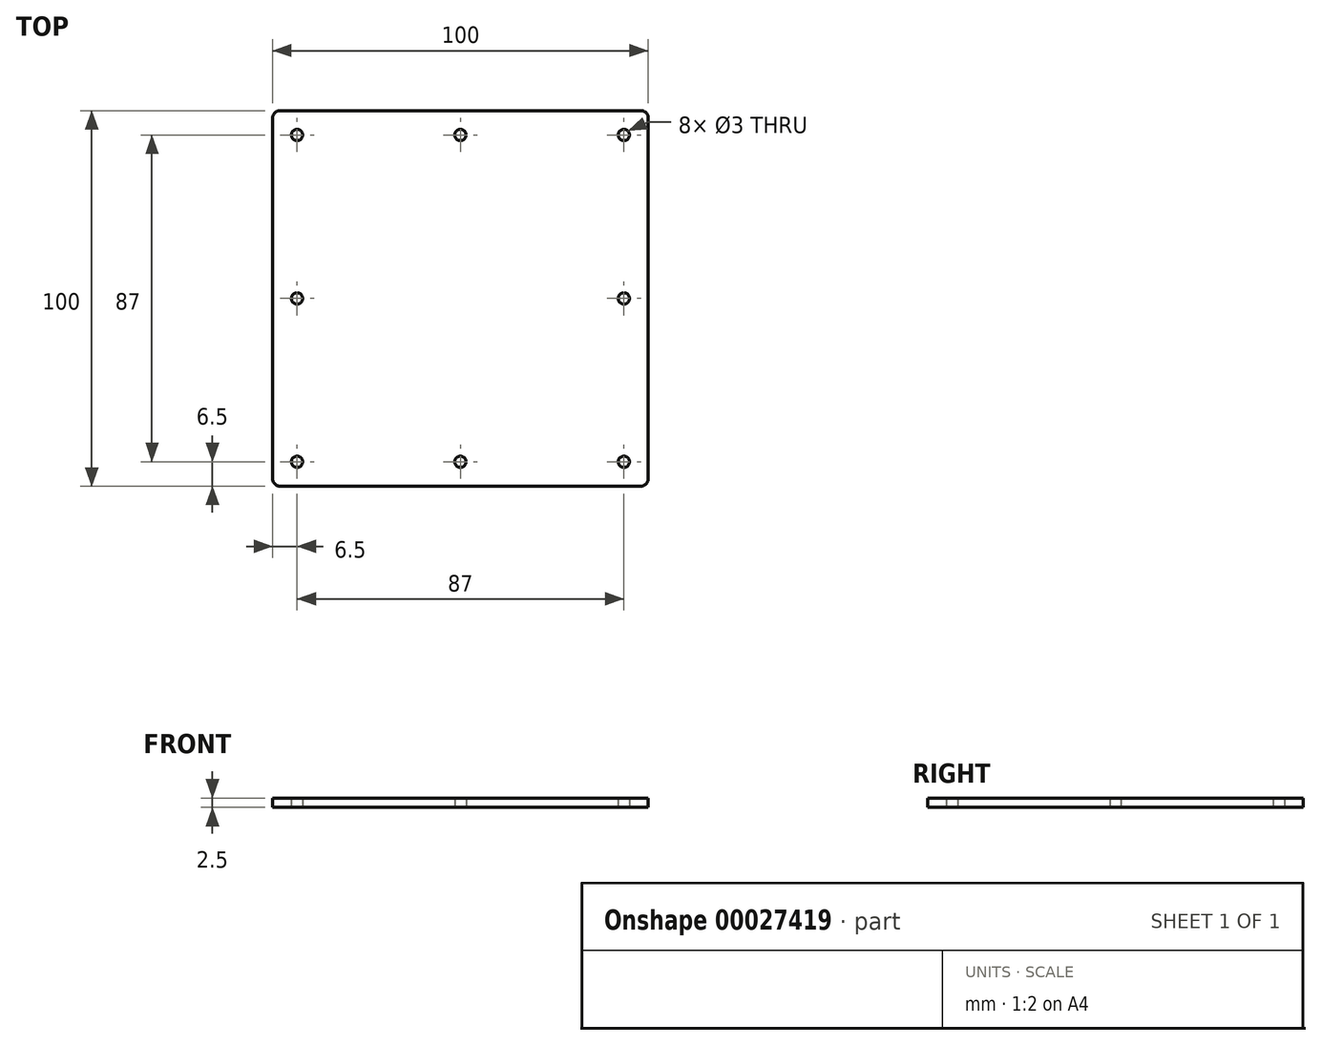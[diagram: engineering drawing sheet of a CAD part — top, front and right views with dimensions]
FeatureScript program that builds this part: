
annotation { "Feature Type Name" : "Feature", "Feature Type Description" : "" }
export const myFeature = defineFeature(function(context is Context, id is Id, definition is map)
    precondition{}
    {
        {
            var Q0;
            Q0=qCreatedBy(makeId("Top.planeOp"),FACE);
            var sketch = newSketch(context, id + "F0", { "sketchPlane" : qUnion([Q0])});
            skLineSegment(sketch, "E0.rect.bottom", {"start": v(50, -50) * mm, "end": v(-50, -50) * mm});
            skLineSegment(sketch, "E0.rect.top", {"start": v(50, 50) * mm, "end": v(-50, 50) * mm});
            skLineSegment(sketch, "E0.rect.left", {"start": v(50, -50) * mm, "end": v(50, 50) * mm});
            skLineSegment(sketch, "E0.rect.right", {"start": v(-50, -50) * mm, "end": v(-50, 50) * mm});
            skPoint(sketch, "E0.rect.middle", {"position": v(0, 0) * mm});
            skLineSegment(sketch, "E1", {"start": v(50, 45) * mm, "end": v(-50, 45) * mm, "construction": true});
            skLineSegment(sketch, "E2", {"start": v(45, 50) * mm, "end": v(45, -50) * mm, "construction": true});
            skCircle(sketch, "E3", {"center": v(-43.5, -43.5) * mm, "radius": 1.5 * mm});
            skCircle(sketch, "E4.MirrorC", {"center": v(43.5, -43.5) * mm, "radius": 1.5 * mm});
            skCircle(sketch, "E5.MirrorC", {"center": v(43.5, 43.5) * mm, "radius": 1.5 * mm});
            skCircle(sketch, "E6.MirrorC", {"center": v(-43.5, 43.5) * mm, "radius": 1.5 * mm});
            skCircle(sketch, "E7", {"center": v(0, 43.5) * mm, "radius": 1.5 * mm});
            skCircle(sketch, "E8.MirrorC", {"center": v(0, -43.5) * mm, "radius": 1.5 * mm});
            skCircle(sketch, "E9", {"center": v(-43.5, 0) * mm, "radius": 1.5 * mm});
            skCircle(sketch, "E10.MirrorC", {"center": v(43.5, 0) * mm, "radius": 1.5 * mm});
            skSolve(sketch);
        }
        {
            var Q0;
            Q0=makeQuery(id+"F0.imprint","IMPRINT",FACE,{"disambiguationData":[TD([[makeQuery(id+"F0.imprint","IMPRINT",EDGE,{"derivedFrom":sQuery(id+"F0.wireOp",EDGE,"E0.rect.bottom")}),-1.0]])]});
            extrude(context, id + "F1", {"entities" : qUnion([Q0]), "depth" : 2.5 * mm});
        }
        {
            var Q0;
            Q0=makeQuery(id+"F1.opExtrude","SWEPT_EDGE",EDGE,{"disambiguationData":[OSD([sQuery(id+"F0.wireOp",EDGE,"E0.rect.bottom"),sQuery(id+"F0.wireOp",EDGE,"E0.rect.right")])]});
            var Q1;
            Q1=makeQuery(id+"F1.opExtrude","SWEPT_EDGE",EDGE,{"disambiguationData":[OSD([sQuery(id+"F0.wireOp",EDGE,"E0.rect.bottom"),sQuery(id+"F0.wireOp",EDGE,"E0.rect.left")])]});
            var Q2;
            Q2=makeQuery(id+"F1.opExtrude","SWEPT_EDGE",EDGE,{"disambiguationData":[OSD([sQuery(id+"F0.wireOp",EDGE,"E0.rect.top"),sQuery(id+"F0.wireOp",EDGE,"E0.rect.left")])]});
            var Q3;
            Q3=makeQuery(id+"F1.opExtrude","SWEPT_EDGE",EDGE,{"disambiguationData":[OSD([sQuery(id+"F0.wireOp",EDGE,"E0.rect.top"),sQuery(id+"F0.wireOp",EDGE,"E0.rect.right")])]});
            fillet(context, id + "F2", {"entities" : qUnion([Q0, Q1, Q2, Q3]), "radius" : 2 * mm, "tangentPropagation" : true, "allowEdgeOverflow" : false});
        }
    });
